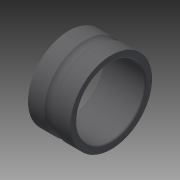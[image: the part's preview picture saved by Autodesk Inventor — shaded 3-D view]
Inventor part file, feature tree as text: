
AUTODESK INVENTOR PART (.ipt)
format: ipt  version: 2014 SP2 (Build 180246200, 246)  size: 167,424 bytes
history: native  units: mm
features: other x112, revolve x1, sketch x1
ambient origin geometry x8: Origin, YZ Plane, XZ Plane, XY Plane, X Axis, Y Axis, Z Axis, Center Point
bodies: Solid1 (feature_tree)
feature tree (114):
  revolve  "Revolution1"  [1 undecoded]
  other  "ip_st_1_1_XY"
  other  "ip_st_1_1_YZ"
  other  "ip_st_1_1_ZX"
  other  "ip_st_1_1_X"
  other  "ip_st_1_1_Y"
  other  "ip_st_1_1_Z"
  other  "ip_st_1_1_Center"
  other  "ip_st_1_10_XY"
  other  "ip_st_1_10_YZ"
  other  "ip_st_1_10_ZX"
  other  "ip_st_1_10_X"
  other  "ip_st_1_10_Y"
  other  "ip_st_1_10_Z"
  other  "ip_st_1_10_Center"
  other  "ip_st_1_11_XY"
  other  "ip_st_1_11_YZ"
  other  "ip_st_1_11_ZX"
  other  "ip_st_1_11_X"
  other  "ip_st_1_11_Y"
  other  "ip_st_1_11_Z"
  other  "ip_st_1_11_Center"
  other  "ip_st_1_12_XY"
  other  "ip_st_1_12_YZ"
  other  "ip_st_1_12_ZX"
  other  "ip_st_1_12_X"
  other  "ip_st_1_12_Y"
  other  "ip_st_1_12_Z"
  other  "ip_st_1_12_Center"
  other  "ip_st_1_13_XY"
  other  "ip_st_1_13_YZ"
  other  "ip_st_1_13_ZX"
  other  "ip_st_1_13_X"
  other  "ip_st_1_13_Y"
  other  "ip_st_1_13_Z"
  other  "ip_st_1_13_Center"
  other  "ip_st_1_14_XY"
  other  "ip_st_1_14_YZ"
  other  "ip_st_1_14_ZX"
  other  "ip_st_1_14_X"
  other  "ip_st_1_14_Y"
  other  "ip_st_1_14_Z"
  other  "ip_st_1_14_Center"
  other  "ip_st_1_2_XY"
  other  "ip_st_1_2_YZ"
  other  "ip_st_1_2_ZX"
  other  "ip_st_1_2_X"
  other  "ip_st_1_2_Y"
  other  "ip_st_1_2_Z"
  other  "ip_st_1_2_Center"
  other  "ip_st_1_3_XY"
  other  "ip_st_1_3_YZ"
  other  "ip_st_1_3_ZX"
  other  "ip_st_1_3_X"
  other  "ip_st_1_3_Y"
  other  "ip_st_1_3_Z"
  other  "ip_st_1_3_Center"
  other  "ip_st_1_4_XY"
  other  "ip_st_1_4_YZ"
  other  "ip_st_1_4_ZX"
  other  "ip_st_1_4_X"
  other  "ip_st_1_4_Y"
  other  "ip_st_1_4_Z"
  other  "ip_st_1_4_Center"
  other  "ip_st_1_5_XY"
  other  "ip_st_1_5_YZ"
  other  "ip_st_1_5_ZX"
  other  "ip_st_1_5_X"
  other  "ip_st_1_5_Y"
  other  "ip_st_1_5_Z"
  other  "ip_st_1_5_Center"
  other  "ip_st_1_6_XY"
  other  "ip_st_1_6_YZ"
  other  "ip_st_1_6_ZX"
  other  "ip_st_1_6_X"
  other  "ip_st_1_6_Y"
  other  "ip_st_1_6_Z"
  other  "ip_st_1_6_Center"
  other  "ip_st_1_7_XY"
  other  "ip_st_1_7_YZ"
  other  "ip_st_1_7_ZX"
  other  "ip_st_1_7_X"
  other  "ip_st_1_7_Y"
  other  "ip_st_1_7_Z"
  other  "ip_st_1_7_Center"
  other  "ip_st_1_8_XY"
  other  "ip_st_1_8_YZ"
  other  "ip_st_1_8_ZX"
  other  "ip_st_1_8_X"
  other  "ip_st_1_8_Y"
  other  "ip_st_1_8_Z"
  other  "ip_st_1_8_Center"
  other  "ip_st_1_9_XY"
  other  "ip_st_1_9_YZ"
  other  "ip_st_1_9_ZX"
  other  "ip_st_1_9_X"
  other  "ip_st_1_9_Y"
  other  "ip_st_1_9_Z"
  other  "ip_st_1_9_Center"
  other  "ip_st_1a_XY"
  other  "ip_st_1a_YZ"
  other  "ip_st_1a_ZX"
  other  "ip_st_1a_X"
  other  "ip_st_1a_Y"
  other  "ip_st_1a_Z"
  other  "ip_st_1a_Center"
  other  "ip_st_2a_XY"
  other  "ip_st_2a_YZ"
  other  "ip_st_2a_ZX"
  other  "ip_st_2a_X"
  other  "ip_st_2a_Y"
  other  "ip_st_2a_Z"
  other  "ip_st_2a_Center"
  sketch  "Sketch_1"  dims[d0=360.0deg d1=0.0mm]
note: 1 required parameter value undecoded (feature->parameter linkage not recoverable at this tier; creation-order binding heuristic only, values carry confidence <= 0.55)
